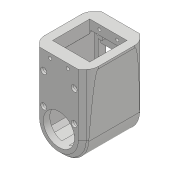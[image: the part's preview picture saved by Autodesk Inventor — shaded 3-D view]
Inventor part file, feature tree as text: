
AUTODESK INVENTOR PART (.ipt)
format: ipt  version: 2018 (Build 220112000, 112)  size: 788,992 bytes
history: native  units: mm
features: sketch x33, projected_geometry x31, extrude x26, hole x9, fillet x7, chamfer x3, mirror x1
ambient origin geometry x8: Origin, YZ Plane, XZ Plane, XY Plane, X Axis, Y Axis, Z Axis, Center Point
bodies: Solid1 (feature_tree)
feature tree (110):
  extrude  "Extrusion1"  Depth=45.0mm
  extrude  "Extrusion2"  Depth=2.25mm
  hole  "Hole1"  [1 undecoded]
  hole  "Hole2"  [1 undecoded]
  fillet  "Fillet1"  Radius=14.0mm
  extrude  "Extrusion3"  Depth=18.5mm
  extrude  "Extrusion4"  Depth=10.0mm
  extrude  "Extrusion5"  Depth=2.0mm
  extrude  "Extrusion6"  Depth=2.0mm
  hole  "Hole3"  [1 undecoded]
  extrude  "Extrusion7"  Depth=0.5mm
  extrude  "Extrusion8"  Depth=5.0mm TaperAngle=0.0deg
  extrude  "Extrusion9"  Depth=10.0mm
  extrude  "Extrusion10"  Depth=10.0mm
  extrude  "Extrusion11"  Depth=14.5mm
  extrude  "Extrusion12"  Depth=20.0mm
  extrude  "Extrusion13"  Depth=5.0mm
  extrude  "Extrusion14"  Depth=5.0mm
  extrude  "Extrusion15"  Depth=5.0mm
  extrude  "Extrusion16"  Depth=5.0mm
  extrude  "Extrusion17"  Depth=1.0mm
  chamfer  "Chamfer1"  Distance=1.0mm
  fillet  "Fillet7"  Radius=20.7mm
  fillet  "Fillet8"  Radius=32.0mm
  mirror  "Mirror1"
  extrude  "Extrusion19"  Depth=1.0mm TaperAngle=0.0deg
  extrude  "Extrusion20"  Depth=8.0mm
  extrude  "Extrusion21"  Depth=0.2mm TaperAngle=0.0deg
  extrude  "Extrusion22"  Depth=0.5mm TaperAngle=0.0deg
  extrude  "Extrusion23"  Depth=5.0mm TaperAngle=0.0deg
  chamfer  "Chamfer2"  Distance=5.0mm
  fillet  "Fillet9"  Radius=0.2mm
  extrude  "Extrusion24"  Depth=2.0mm TaperAngle=45.0deg
  extrude  "Extrusion27"  Depth=0.5mm
  extrude  "Extrusion28"  Depth=1.8mm TaperAngle=0.0deg
  hole  "Hole6"  [1 undecoded]
  sketch  "Sketch39"  dims[d105=1.5mm d114=0.5mm]
  hole  "Hole7"  [1 undecoded]
  hole  "Hole8"  [1 undecoded]
  fillet  "Fillet10"  Radius=2.0mm
  hole  "Hole9"  [1 undecoded]
  extrude  "Extrusion29"  Depth=0.75mm
  chamfer  "Chamfer4"  Distance=33.0mm
  hole  "Hole10"  [1 undecoded]
  fillet  "Fillet11"  Radius=20.75mm
  hole  "Hole11"  [1 undecoded]
  fillet  "Fillet12"  Radius=25.0mm
  sketch  "Sketch1"  dims[d0=24.5mm d1=45.0mm]
  sketch  "Sketch2"  dims[d2=1.95mm d3=0.0mm d4=2.25mm]
  projected_geometry  "Projected Loop1"
  sketch  "Sketch3"  dims[d5=20.0mm d6=2.25mm]
  projected_geometry  "Projected Loop2"
  sketch  "Sketch4"  dims[d7=5.25mm d8=5.25mm d9=14.0mm]
  projected_geometry  "Projected Loop3"
  sketch  "Sketch5"  dims[d10=5.25mm d11=18.5mm]
  projected_geometry  "Projected Loop4"
  sketch  "Sketch6"  dims[d12=10.0mm d13=0.0mm d14=20.5mm]
  projected_geometry  "Projected Loop5"
  sketch  "Sketch7"  dims[d15=2.0mm d16=2.195mm]
  projected_geometry  "Projected Loop6"
  sketch  "Sketch8"  dims[d17=2.0mm]
  projected_geometry  "Projected Loop7"
  sketch  "Sketch9"  dims[d18=2.4mm d19=6.0mm d20=4.4mm d21=2.0mm d22=90.0deg d23=8.0mm d24=20.594885mm d25=20.5mm]
  projected_geometry  "Projected Loop8"
  projected_geometry  "Projected Loop9"
  sketch  "Sketch10"  dims[d26=26.65mm d27=2.0mm]
  projected_geometry  "Projected Loop10"
  projected_geometry  "Projected Loop11"
  sketch  "Sketch11"  dims[d28=2.0mm]
  projected_geometry  "Projected Loop12"
  sketch  "Sketch12"  dims[d29=2.4mm d30=6.0mm d31=4.4mm d32=2.0mm d33=90.0deg d34=8.0mm d35=20.594885mm d36=0.5mm]
  sketch  "Sketch13"  dims[d37=18.0mm d38=5.0mm d39=0.0mm]
  sketch  "Sketch14"  dims[d41=10.0mm d42=0.0mm d43=24.5mm]
  projected_geometry  "Projected Loop13"
  sketch  "Sketch15"  dims[d44=1.15mm d45=0.0mm d46=10.0mm]
  sketch  "Sketch16"  dims[d47=21.0mm d48=14.5mm]
  projected_geometry  "Projected Loop14"
  sketch  "Sketch17"  dims[d49=20.0mm d50=14.5mm]
  projected_geometry  "Projected Loop15"
  sketch  "Sketch18"  dims[d51=24.5mm d52=5.0mm]
  projected_geometry  "Projected Loop16"
  sketch  "Sketch19"  dims[d53=5.0mm d54=2.25mm]
  projected_geometry  "Projected Loop17"
  sketch  "Sketch20"  dims[d55=2.25mm d56=5.0mm]
  projected_geometry  "Projected Loop18"
  sketch  "Sketch25"  dims[d57=5.0mm d58=9.0mm]
  projected_geometry  "Projected Loop22"
  sketch  "Sketch26"  dims[d59=14.75mm d60=4.0mm d61=1.0mm d62=0.0mm d63=20.7mm]
  projected_geometry  "Projected Loop23"
  sketch  "Sketch27"  dims[d64=2.4mm d65=6.0mm d66=4.4mm d67=2.0mm d68=90.0deg d69=8.0mm d70=20.594885mm d72=32.0mm]
  projected_geometry  "Projected Loop25"
  sketch  "Sketch29"  dims[d73=5.0mm d74=0.0mm d75=1.0mm d76=0.0mm]
  projected_geometry  "Projected Loop26"
  sketch  "Sketch30"  dims[d77=12.25mm d78=0.0mm d80=8.0mm]
  projected_geometry  "Projected Loop27"
  sketch  "Sketch32"  dims[d81=4.5mm d82=0.0mm d84=0.2mm d85=0.0mm]
  projected_geometry  "Projected Loop28"
  projected_geometry  "Projected Loop29"
  sketch  "Sketch36"  dims[d86=21.0mm d87=0.5mm d88=0.0mm]
  projected_geometry  "Projected Loop33"
  sketch  "Sketch37"  dims[d91=8.0mm d92=0.0mm d93=5.0mm d94=0.0mm d95=5.0mm d96=0.0mm d98=0.2mm d99=0.0mm]
  projected_geometry  "Projected Loop34"
  sketch  "Sketch38"  dims[d100=0.2mm d101=0.0mm d102=2.5mm d103=2.0mm d104=45.0deg]
  projected_geometry  "Projected Loop35"
  sketch  "Sketch41"  dims[d128=1.8mm d129=0.0mm d130=1.8mm d131=0.0mm]
  projected_geometry  "Projected Loop36"
  sketch  "Sketch42"  dims[d133=36.055mm d134=4.2225mm]
  projected_geometry  "Projected Loop37"
  sketch  "Sketch43"  dims[d135=4.2225mm d136=2.0mm d137=0.0mm d138=2.0mm d139=0.0mm d140=2.0mm d141=0.0mm d142=5.0mm d143=2.0mm d144=45.0deg d145=8.0mm d147=33.0mm d148=10.0mm d149=0.0mm d161=20.75mm d162=18.0mm d163=25.0mm d164=0.05mm d165=7.0mm d166=0.0mm d167=1.5mm d168=0.0mm d169=3.0mm d170=12.0mm d171=2.1mm d172=6.0mm d173=6.3mm d174=2.0mm d175=90.0deg d176=8.0mm d177=20.594885mm d178=1.567mm d179=36.0mm d180=4.4mm d181=2.0mm d182=90.0deg d183=36.0mm d184=20.594885mm d185=4.0mm d186=5.029mm d187=4.4mm d188=2.0mm d189=90.0deg d190=15.0mm d191=0.0mm d192=0.5mm d193=2.1mm d194=5.029mm d195=4.4mm d196=2.0mm d197=90.0deg d198=20.75mm d199=0.0mm d200=15.0mm d201=1.5mm d202=0.0mm d203=1.5mm d204=2.0mm d205=45.0deg d206=4.0mm d207=5.029mm d208=4.4mm d209=2.0mm d210=90.0deg d211=2.2mm d212=0.0mm d213=0.75mm d214=4.0mm d215=5.029mm d216=4.4mm d217=2.0mm d218=90.0deg d219=2.2mm d220=0.0mm d221=0.75mm]
  projected_geometry  "Projected Loop38"
note: 9 required parameter values undecoded (feature->parameter linkage not recoverable at this tier; creation-order binding heuristic only, values carry confidence <= 0.55)
